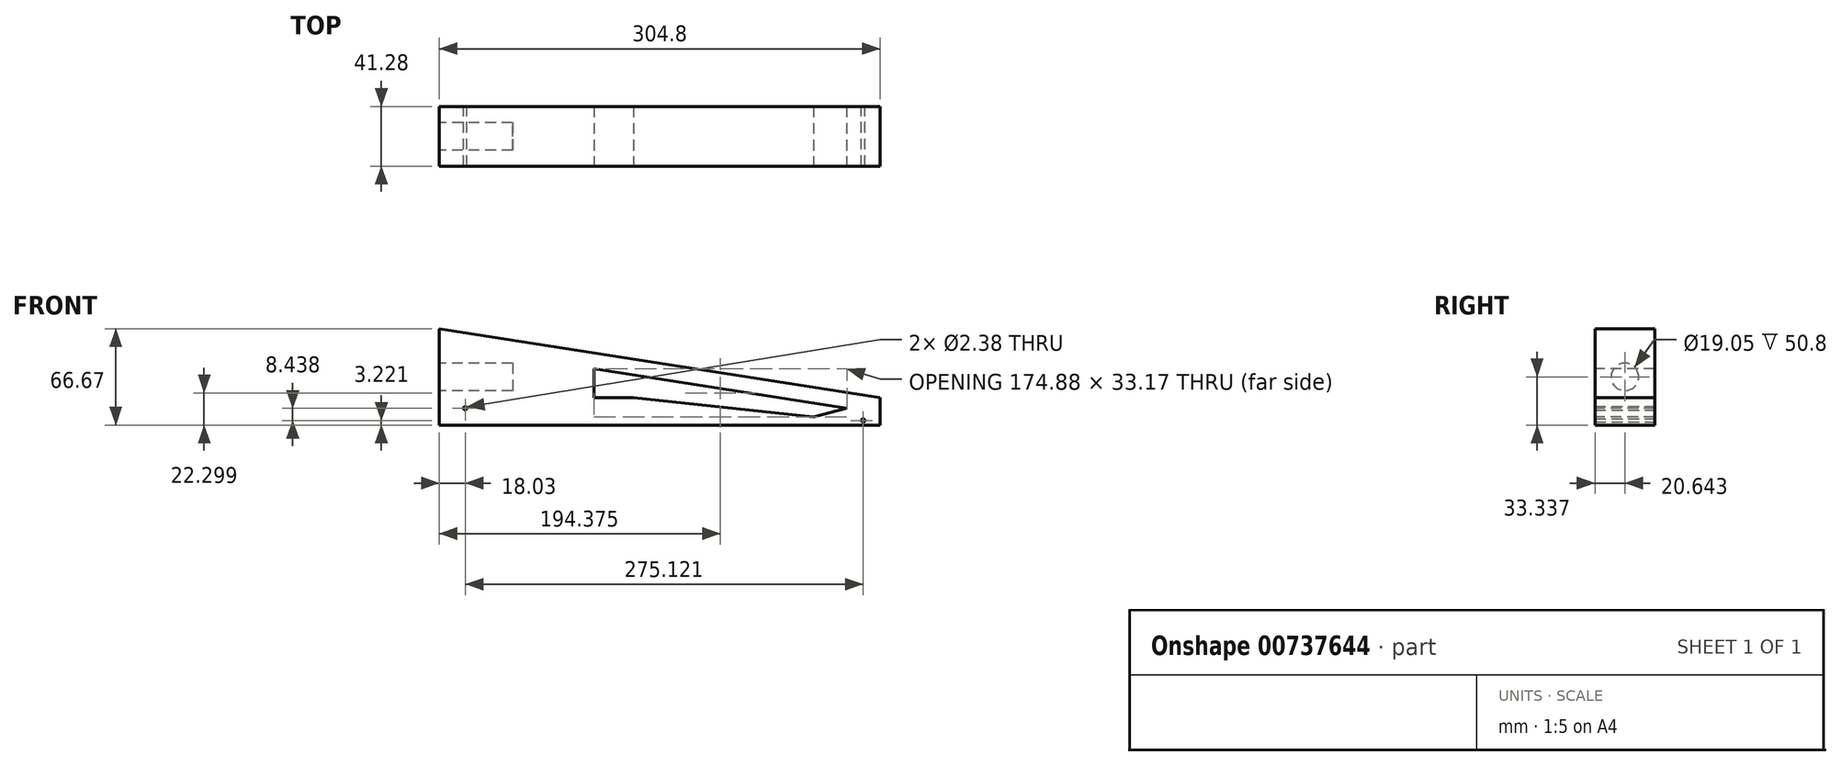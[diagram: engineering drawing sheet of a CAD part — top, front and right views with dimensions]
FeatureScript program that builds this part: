
annotation { "Feature Type Name" : "Feature", "Feature Type Description" : "" }
export const myFeature = defineFeature(function(context is Context, id is Id, definition is map)
    precondition{}
    {
        {
            var Q0;
            Q0=qCreatedBy(makeId("Front.planeOp"),FACE);
            var sketch = newSketch(context, id + "F0", { "sketchPlane" : qUnion([Q0])});
            skLineSegment(sketch, "E0", {"start": v(-152.97, 0) * mm, "end": v(151.83, 0) * mm});
            skLineSegment(sketch, "E1", {"start": v(-152.97, 0) * mm, "end": v(-152.97, 66.68) * mm});
            skLineSegment(sketch, "E2", {"start": v(151.83, 0) * mm, "end": v(151.83, 19.05) * mm});
            skLineSegment(sketch, "E3", {"start": v(-152.97, 66.68) * mm, "end": v(151.83, 19.05) * mm});
            skSolve(sketch);
        }
        {
            var Q0;
            Q0=makeQuery(id+"F0.imprint","IMPRINT",FACE,{"disambiguationData":[TD([[makeQuery(id+"F0.imprint","IMPRINT",EDGE,{"derivedFrom":sQuery(id+"F0.wireOp",EDGE,"E0")}),1.0]])]});
            extrude(context, id + "F1", {"entities" : qUnion([Q0]), "depth" : 41.27 * mm, "offsetDistance" : 25.4 * mm});
        }
        {
            var Q0;
            Q0=makeQuery(id+"F1.opExtrude","SWEPT_FACE",FACE,{"disambiguationData":[OSD([sQuery(id+"F0.wireOp",EDGE,"E1")])]});
            var sketch = newSketch(context, id + "F2", { "sketchPlane" : qUnion([Q0])});
            skCircle(sketch, "E4", {"center": v(20.64, 33.34) * mm, "radius": 9.53 * mm});
            skSolve(sketch);
        }
        {
            var Q0;
            Q0=makeQuery(id+"F2.imprint","IMPRINT",FACE,{"disambiguationData":[TD([[makeQuery(id+"F2.imprint","IMPRINT",EDGE,{"derivedFrom":sQuery(id+"F2.wireOp",EDGE,"E4")}),1.0]])]});
            extrude(context, id + "F3", {"entities" : qUnion([Q0]), "operationType" : NewBodyOperationType.REMOVE, "oppositeDirection" : true, "depth" : 50.8 * mm, "offsetDistance" : 25.4 * mm});
        }
        {
            var Q0;
            Q0=makeQuery(id+"F1.opExtrude","CAP_FACE",FACE,{"disambiguationData":[OSD([sQuery(id+"F0.wireOp",EDGE,"E0"),sQuery(id+"F0.wireOp",EDGE,"E1"),sQuery(id+"F0.wireOp",EDGE,"E2"),sQuery(id+"F0.wireOp",EDGE,"E3")])],"isStart":false});
            var sketch = newSketch(context, id + "F4", { "sketchPlane" : qUnion([Q0])});
            skLineSegment(sketch, "E5", {"start": v(128.85, 11.56) * mm, "end": v(2.08, 31.36) * mm});
            skLineSegment(sketch, "E6", {"start": v(2.08, 31.36) * mm, "end": v(-18.73, 19.05) * mm});
            skLineSegment(sketch, "E7", {"start": v(-18.73, 19.05) * mm, "end": v(105.73, 5.72) * mm});
            skLineSegment(sketch, "E8", {"start": v(105.73, 5.72) * mm, "end": v(128.85, 11.56) * mm});
            skSolve(sketch);
        }
        {
            var Q0;
            Q0=makeQuery(id+"F4.imprint","IMPRINT",FACE,{"disambiguationData":[TD([[makeQuery(id+"F4.imprint","IMPRINT",EDGE,{"derivedFrom":sQuery(id+"F4.wireOp",EDGE,"E5")}),1.0]])]});
            extrude(context, id + "F5", {"entities" : qUnion([Q0]), "operationType" : NewBodyOperationType.REMOVE, "oppositeDirection" : true, "depth" : 45.72 * mm, "offsetDistance" : 25.4 * mm});
        }
        {
            var Q0;
            Q0=makeQuery(id+"F1.opExtrude","CAP_FACE",FACE,{"disambiguationData":[OSD([sQuery(id+"F0.wireOp",EDGE,"E0"),sQuery(id+"F0.wireOp",EDGE,"E1"),sQuery(id+"F0.wireOp",EDGE,"E2"),sQuery(id+"F0.wireOp",EDGE,"E3")])],"isStart":false});
            var sketch = newSketch(context, id + "F6", { "sketchPlane" : qUnion([Q0])});
            skLineSegment(sketch, "E9", {"start": v(2.08, 31.36) * mm, "end": v(-46.04, 38.88) * mm});
            skLineSegment(sketch, "E10", {"start": v(-46.04, 38.88) * mm, "end": v(-18.73, 19.05) * mm});
            skLineSegment(sketch, "E11", {"start": v(-18.73, 19.05) * mm, "end": v(-46.04, 19.05) * mm});
            skLineSegment(sketch, "E12", {"start": v(-46.04, 19.05) * mm, "end": v(-46.04, 38.88) * mm});
            skSolve(sketch);
        }
        {
            var Q0;
            Q0=makeQuery(id+"F6.imprint","IMPRINT",FACE,{"disambiguationData":[TD([[makeQuery(id+"F6.imprint","IMPRINT",EDGE,{"derivedFrom":sQuery(id+"F6.wireOp",EDGE,"E10")}),-1.0]])]});
            var Q1;
            Q1=makeQuery(id+"F6.imprint","IMPRINT",FACE,{"disambiguationData":[TD([[makeQuery(id+"F6.imprint","IMPRINT",EDGE,{"derivedFrom":sQuery(id+"F6.wireOp",EDGE,"E9")}),1.0]])]});
            extrude(context, id + "F7", {"entities" : qUnion([Q0, Q1]), "operationType" : NewBodyOperationType.REMOVE, "oppositeDirection" : true, "depth" : 60.96 * mm, "offsetDistance" : 25.4 * mm});
        }
        {
            var Q0;
            Q0=makeQuery(id+"F1.opExtrude","CAP_FACE",FACE,{"disambiguationData":[OSD([sQuery(id+"F0.wireOp",EDGE,"E0"),sQuery(id+"F0.wireOp",EDGE,"E1"),sQuery(id+"F0.wireOp",EDGE,"E2"),sQuery(id+"F0.wireOp",EDGE,"E3")])],"isStart":true});
            var sketch = newSketch(context, id + "F8", { "sketchPlane" : qUnion([Q0])});
            skCircle(sketch, "E13", {"center": v(134.94, 11.66) * mm, "radius": 1.2 * mm});
            skSolve(sketch);
        }
        {
            var Q0;
            Q0=makeQuery(id+"F8.imprint","IMPRINT",FACE,{"disambiguationData":[TD([[makeQuery(id+"F8.imprint","IMPRINT",EDGE,{"derivedFrom":sQuery(id+"F8.wireOp",EDGE,"E13")}),1.0]])]});
            extrude(context, id + "F9", {"entities" : qUnion([Q0]), "operationType" : NewBodyOperationType.REMOVE, "oppositeDirection" : true, "depth" : 63.5 * mm, "offsetDistance" : 25.4 * mm});
        }
        {
            var Q0;
            Q0=makeQuery(id+"F1.opExtrude","CAP_FACE",FACE,{"disambiguationData":[OSD([sQuery(id+"F0.wireOp",EDGE,"E0"),sQuery(id+"F0.wireOp",EDGE,"E1"),sQuery(id+"F0.wireOp",EDGE,"E2"),sQuery(id+"F0.wireOp",EDGE,"E3")])],"isStart":true});
            var sketch = newSketch(context, id + "F10", { "sketchPlane" : qUnion([Q0])});
            skCircle(sketch, "E14", {"center": v(-140.18, 3.22) * mm, "radius": 1.2 * mm});
            skSolve(sketch);
        }
        {
            var Q0;
            Q0=makeQuery(id+"F10.imprint","IMPRINT",FACE,{"disambiguationData":[TD([[makeQuery(id+"F10.imprint","IMPRINT",EDGE,{"derivedFrom":sQuery(id+"F10.wireOp",EDGE,"E14")}),1.0]])]});
            extrude(context, id + "F11", {"entities" : qUnion([Q0]), "operationType" : NewBodyOperationType.REMOVE, "oppositeDirection" : true, "depth" : 63.5 * mm, "offsetDistance" : 25.4 * mm});
        }
    });
